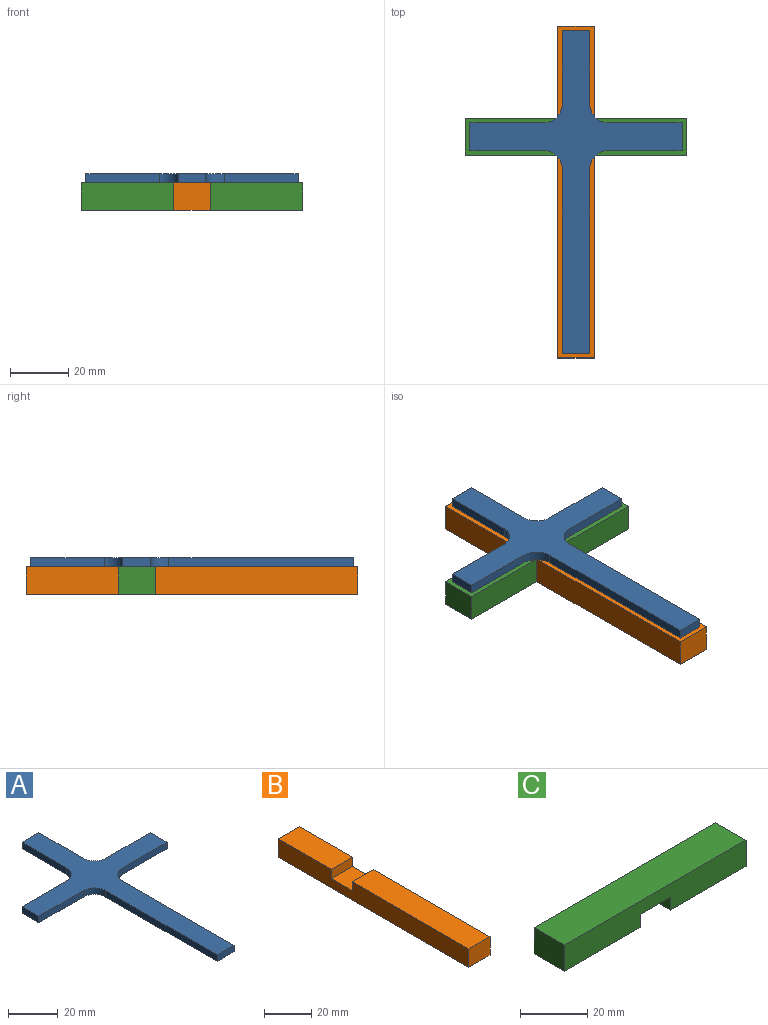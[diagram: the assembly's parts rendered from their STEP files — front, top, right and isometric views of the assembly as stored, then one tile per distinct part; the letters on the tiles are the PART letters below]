
ASSEMBLY  parts=3 mates=2
PART A: 18 faces, bbox 73x111.1x3.2 mm
  f0: plane 25.4x3.18mm, normal (0,-1,0), area 80.6mm2, adj f1,f15,f16,f17
  f1: cylinder r=6.35mm len=6.35mm, axis (0,0,-1), area 31.7mm2, adj f0,f2,f16,f17
  f2: plane 63.5x3.18mm, normal (-1,0,0), area 201.6mm2, adj f1,f3,f16,f17
  f3: plane 9.53x3.18mm, normal (0,-1,0), area 30.2mm2, adj f2,f4,f16,f17
  f4: plane 63.5x3.18mm, normal (1,0,0), area 201.6mm2, adj f3,f5,f16,f17
  f5: cylinder r=6.35mm len=6.35mm, axis (0,0,-1), area 31.7mm2, adj f4,f6,f16,f17
  f6: plane 25.4x3.18mm, normal (0,-1,0), area 80.6mm2, adj f5,f7,f16,f17
  f7: plane 9.53x3.18mm, normal (1,0,0), area 30.2mm2, adj f6,f8,f16,f17
  f8: plane 25.4x3.18mm, normal (0,1,0), area 80.6mm2, adj f7,f9,f16,f17
  f9: cylinder r=6.35mm len=6.35mm, axis (0,0,-1), area 31.7mm2, adj f8,f10,f16,f17
  f10: plane 25.4x3.18mm, normal (1,0,0), area 80.6mm2, adj f9,f11,f16,f17
  f11: plane 9.53x3.18mm, normal (0,1,0), area 30.2mm2, adj f10,f12,f16,f17
  f12: plane 25.4x3.18mm, normal (-1,0,0), area 80.6mm2, adj f11,f13,f16,f17
  f13: cylinder r=6.35mm len=6.35mm, axis (0,0,-1), area 31.7mm2, adj f12,f14,f16,f17
  f14: plane 25.4x3.18mm, normal (0,1,0), area 80.6mm2, adj f13,f15,f16,f17
  f15: plane 9.53x3.18mm, normal (-1,0,0), area 30.2mm2, adj f0,f14,f16,f17
  f16: plane 111.13x73.03mm, normal (0,0,1), area 1697.9mm2, adj f0,f1,f2,f3,f4,f5,f6,f7
  f17: plane 111.13x73.03mm, normal (0,0,-1), area 1697.9mm2, adj f0,f1,f2,f3,f4,f5,f6,f7
PART B: 10 faces, bbox 12.7x114.3x9.5 mm
  f0: plane 69.85x12.7mm, normal (0,0,1), area 887.1mm2, adj f1,f2,f5,f7
  f1: plane 114.3x9.53mm, normal (1,0,0), area 1028.2mm2, adj f0,f3,f4,f5,f6,f7,f8,f9
  f2: plane 114.3x9.53mm, normal (-1,0,0), area 1028.2mm2, adj f0,f3,f4,f5,f6,f7,f8,f9
  f3: plane 114.3x12.7mm, normal (0,0,-1), area 1451.6mm2, adj f1,f2,f5,f6
  f4: plane 31.75x12.7mm, normal (0,0,1), area 403.2mm2, adj f1,f2,f6,f9
  f5: plane 12.7x9.53mm, normal (0,-1,0), area 121mm2, adj f0,f1,f2,f3
  f6: plane 12.7x9.53mm, normal (0,1,0), area 121mm2, adj f1,f2,f3,f4
  f7: plane 12.7x4.76mm, normal (0,1,0), area 60.5mm2, adj f0,f1,f2,f8
  f8: plane 12.7x12.7mm, normal (0,0,1), area 161.3mm2, adj f1,f2,f7,f9
  f9: plane 12.7x4.76mm, normal (0,-1,0), area 60.5mm2, adj f1,f2,f4,f8
PART C: 10 faces, bbox 76.2x12.7x9.5 mm
  f0: plane 31.75x12.7mm, normal (0,0,-1), area 403.2mm2, adj f1,f2,f6,f7
  f1: plane 76.2x9.53mm, normal (0,1,0), area 665.3mm2, adj f0,f3,f4,f5,f6,f7,f8,f9
  f2: plane 76.2x9.53mm, normal (0,-1,0), area 665.3mm2, adj f0,f3,f4,f5,f6,f7,f8,f9
  f3: plane 31.75x12.7mm, normal (0,0,-1), area 403.2mm2, adj f1,f2,f5,f8
  f4: plane 76.2x12.7mm, normal (0,0,1), area 967.7mm2, adj f1,f2,f5,f6
  f5: plane 12.7x9.53mm, normal (1,0,0), area 121mm2, adj f1,f2,f3,f4
  f6: plane 12.7x9.53mm, normal (-1,0,0), area 121mm2, adj f0,f1,f2,f4
  f7: plane 12.7x4.76mm, normal (1,0,0), area 60.5mm2, adj f0,f1,f2,f9
  f8: plane 12.7x4.76mm, normal (-1,0,0), area 60.5mm2, adj f1,f2,f3,f9
  f9: plane 12.7x12.7mm, normal (0,0,-1), area 161.3mm2, adj f1,f2,f7,f8
PLACE A t=(0,0,4.76)mm
PLACE B at identity
PLACE C at identity
MATE fastened C.f9 <-> B.f8  axis (0,0,1) through (0,0,0)mm
MATE fastened A.f17 <-> C.f4  axis (0,0,1) through (0,0,4.76)mm
